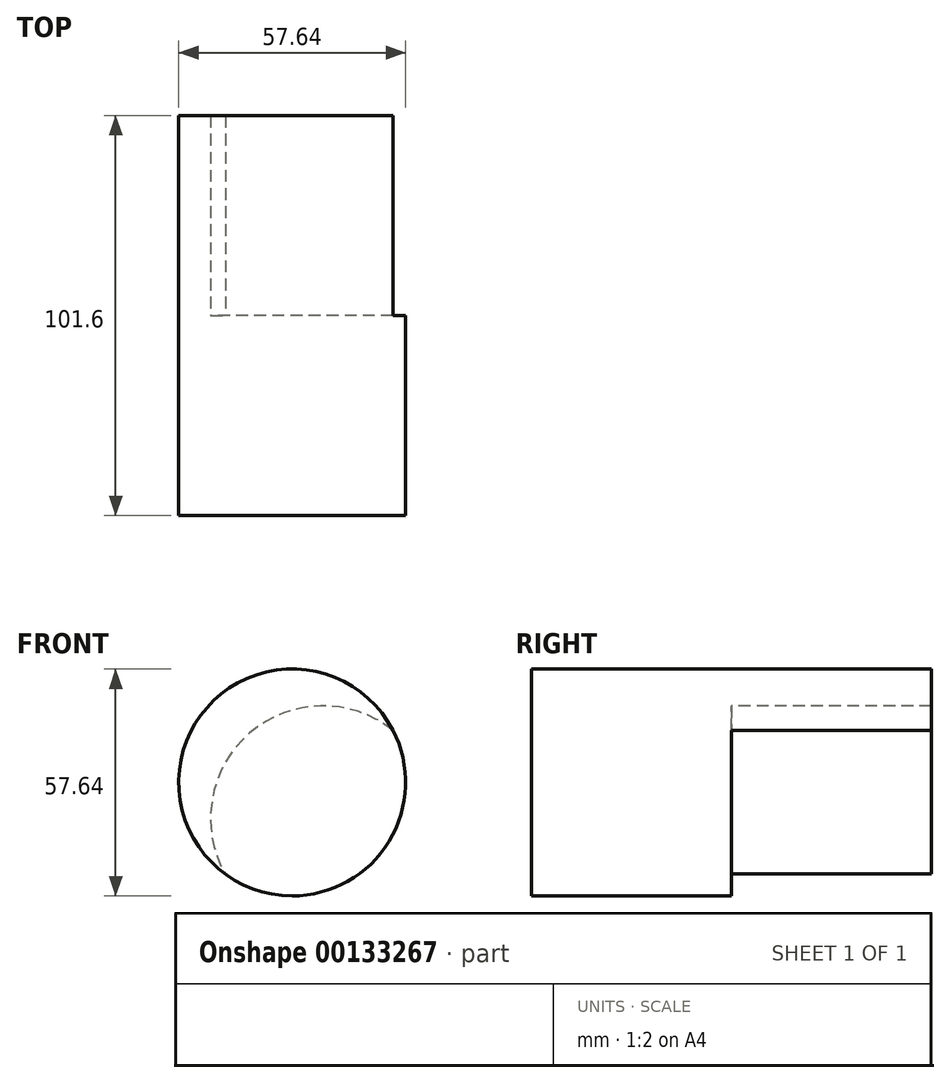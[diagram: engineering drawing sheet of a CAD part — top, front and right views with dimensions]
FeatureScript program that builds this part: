
annotation { "Feature Type Name" : "Feature", "Feature Type Description" : "" }
export const myFeature = defineFeature(function(context is Context, id is Id, definition is map)
    precondition{}
    {
        {
            var Q0;
            Q0=qCreatedBy(makeId("Front.planeOp"),FACE);
            var sketch = newSketch(context, id + "F0", { "sketchPlane" : qUnion([Q0])});
            skCircle(sketch, "E0", {"center": v(0, 0) * mm, "radius": 28.82 * mm});
            skSolve(sketch);
        }
        {
            var Q0;
            Q0 = qSketchRegion(id + "F0", true);
            extrude(context, id + "F1", {"entities" : qUnion([Q0]), "endBound" : BoundingType.SYMMETRIC, "depth" : 101.6 * mm});
        }
        {
            var Q0;
            Q0=qCreatedBy(makeId("Front.planeOp"),FACE);
            var sketch = newSketch(context, id + "F2", { "sketchPlane" : qUnion([Q0])});
            skCircle(sketch, "E1", {"center": v(7.84, -9.13) * mm, "radius": 5.63 * mm});
            skCircle(sketch, "E2", {"center": v(8.7, 7.99) * mm, "radius": 5.62 * mm});
            skCircle(sketch, "E3", {"center": v(-11.48, -8.85) * mm, "radius": 5.66 * mm});
            skCircle(sketch, "E4", {"center": v(-10.52, 7.22) * mm, "radius": 5.33 * mm});
            skSolve(sketch);
        }
        {
            var Q0;
            Q0=sQuery(id+"F2.wireOp",VERTEX,"E1.center");
            var Q1;
            Q1=makeQuery(id+"F1.opExtrude","SWEPT_BODY",BODY,{"disambiguationData":[OSD([sQuery(id+"F0.wireOp",EDGE,"E0")])]});
            hole(context, id + "F3", {"style" : HoleStyle.SIMPLE, "endStyle" : HoleEndStyle.THROUGH, "holeDiameter" : 57.15 * mm, "locations" : qUnion([Q0]), "scope" : qUnion([Q1]), "isTappedThrough" : true});
        }
    });
